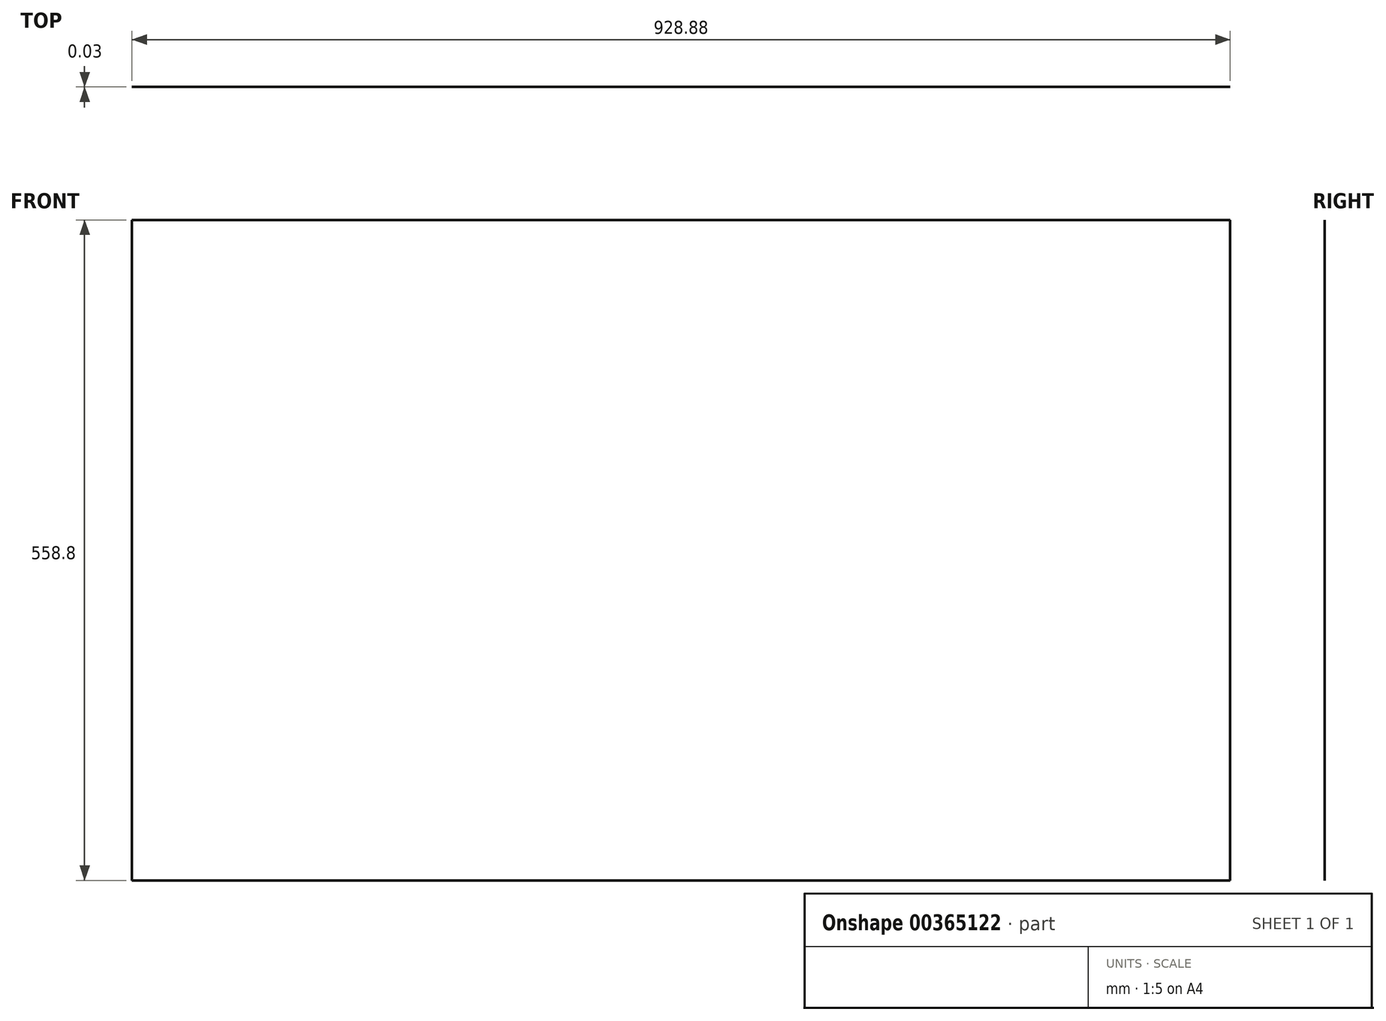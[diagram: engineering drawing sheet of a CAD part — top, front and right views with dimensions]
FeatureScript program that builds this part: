
annotation { "Feature Type Name" : "Feature", "Feature Type Description" : "" }
export const myFeature = defineFeature(function(context is Context, id is Id, definition is map)
    precondition{}
    {
        {
            var Q0;
            Q0=qCreatedBy(makeId("Front.planeOp"),FACE);
            var sketch = newSketch(context, id + "F0", { "sketchPlane" : qUnion([Q0])});
            skLineSegment(sketch, "E0.bottom", {"start": v(0, 0) * mm, "end": v(928.88, 0) * mm});
            skLineSegment(sketch, "E0.top", {"start": v(0, 558.8) * mm, "end": v(928.88, 558.8) * mm});
            skLineSegment(sketch, "E0.left", {"start": v(0, 0) * mm, "end": v(0, 558.8) * mm});
            skLineSegment(sketch, "E0.right", {"start": v(928.88, 0) * mm, "end": v(928.88, 558.8) * mm});
            skSolve(sketch);
        }
        {
            var Q0;
            Q0 = qSketchRegion(id + "F0", true);
            extrude(context, id + "F1", {"entities" : qUnion([Q0]), "flatOperationType" : FlatOperationType.REMOVE, "offsetDistance" : 25.4 * mm, "depth" : 23 / 812.8 * mm, "domain" : OperationDomain.MODEL});
        }
    });
